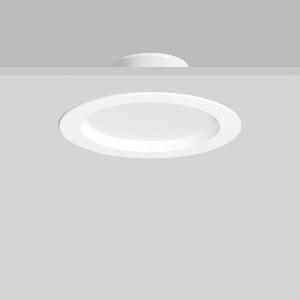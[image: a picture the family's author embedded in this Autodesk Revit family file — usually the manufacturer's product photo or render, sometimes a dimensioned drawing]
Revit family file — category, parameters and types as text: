
# Revit family: hb_801_901697_002_9124
name_source: partatom
category: Lighting Fixtures
units: mm (PartAtom-declared; Revit-internal decimal feet)

## family parameters
Cut with Voids When Loaded = No
Host = Face
Light Source = No
Part Type = Normal
Room Calculation Point = No
Round Connector Dimension = Use Diameter
Shared = No

## types (1)
- MultiColor 840 (1 x LED Modul 840, 1950 lm, 4000)
    Apparent Load = 20 VA
    CIE Flux Codes = 50 82 97 100 100
    Color Rendering = 80
    Color Temperature = 4000
    Default Elevation = 1800 mm
    Description = Series: HB 801
Round recessed downlight. Housing: aluminium, plastic-coated. Passive cooling. Diffuser made of plastic (polycarbonate), opal, shockproof. MultiColour: Colour temperature adjustable via switching element. Choice of 3000 K, 4000 K or 5700 K.Factory setting is 4000 K. Installation without tools thanks to spring fastening system. Driver included. 
Colour: white
Diameter: 225 mm
Height: 3 mm
Cut-out diameter: 205 mm
Recess height: 103 mm
Luminaire: recess height: 83 mm
Lamp: LED
Socket: without socket
Colour temperature: 3000K, 4000K, 5700K
Colour rendering index (CRI): 80
System power: 20 W
Rated luminous flux: 1950 lm
Beam angle Down: 106°
Luminous efficiency: 98 lm/W
System power 2: 20 W
Rated luminous flux 2: 1700 lm
Luminous efficiency 2: 85 lm/W
System power 3: 20 W
Rated luminous flux 3: 1900 lm
Luminous efficiency 3: 95 lm/W
Control gear: Regulated power supply
Protection class: II
Type of protection: IP 54
    Height = 0 mm  [stored 0 ft]
    Lamp = 1 x LED Modul 840
    Lamp Light Flux = 1950 lm
    Lamp count = 1
    Length = 225 mm
    Lifetime = 50000 h
    Luminous efficacy = 98 lm/W
    Manufacturer = RZB
    ModVariant = No
    Model = 901697.002
    Mounting Place = Ceiling
    Mounting Type = Recessed
    Number of Poles = 1
    OnlyDefault = Yes
    Power Factor = 1
    Product Name = HB 801
    Product group = Recessed downlights
    ProductGroupID = 402
    Protection Class = Protection class II
    Protection Degree = IP 54
    RLX_Detail_Level = 1
    RLX_Emergency_Light_Flux = 0 lm
    RLX_Emergency_Type = 0
    RLX_Emergency_Type_DB = No
    RlxData = <blob elided: 32021 chars, md5=05185389>
    Socket = socket
    Standby Power = 0 W
    System Light Flux = 1950 lm
    System Power = 20 W
    Type Comments = MultiColor 840
    Type Image = 901697.002.jpg
    URL = http://relux.com
    VarID = multicolor_840
    Voltage = 0 V
    Weight = 0.00 kg
    Width = 0 mm  [stored 0 ft]

note: [stored X ft] marks values corroborated as IEEE doubles in the binary element streams (Revit-internal decimal feet)

## geometry (parser evidence)
native form markers: Blend x4, Sweep x10
no freeform markers — native parametric forms only
